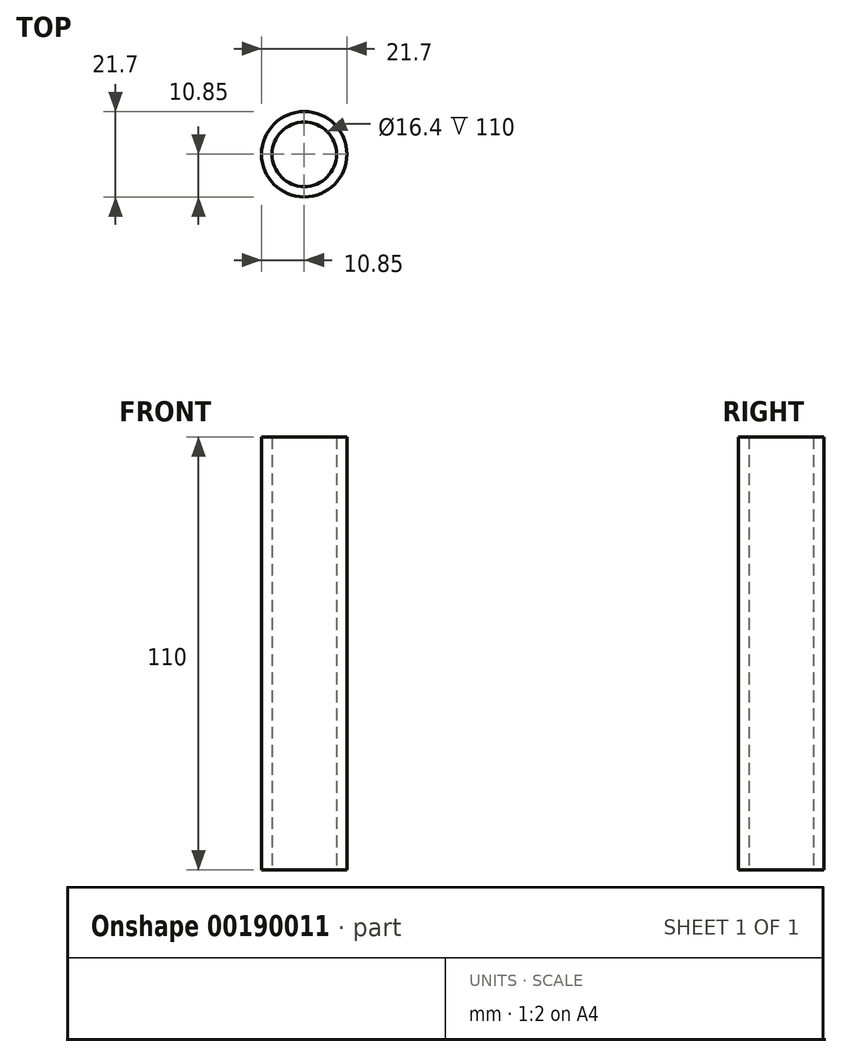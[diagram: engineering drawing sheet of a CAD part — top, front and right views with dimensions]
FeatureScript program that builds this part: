
annotation { "Feature Type Name" : "Feature", "Feature Type Description" : "" }
export const myFeature = defineFeature(function(context is Context, id is Id, definition is map)
    precondition{}
    {
        {
            var Q0;
            Q0=qCreatedBy(makeId("Top.planeOp"),FACE);
            var sketch = newSketch(context, id + "F0", { "sketchPlane" : qUnion([Q0])});
            skCircle(sketch, "E0", {"center": v(0, 0) * mm, "radius": 10.85 * mm});
            skCircle(sketch, "E1.0", {"center": v(0, 0) * mm, "radius": 8.2 * mm});
            skSolve(sketch);
        }
        {
            var Q0;
            Q0=makeQuery(id+"F0.imprint","IMPRINT",FACE,{"disambiguationData":[TD([[makeQuery(id+"F0.imprint","IMPRINT",EDGE,{"derivedFrom":sQuery(id+"F0.wireOp",EDGE,"E0")}),1.0]])]});
            extrude(context, id + "F1", {"entities" : qUnion([Q0]), "depth" : 110 * mm});
        }
    });
